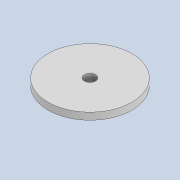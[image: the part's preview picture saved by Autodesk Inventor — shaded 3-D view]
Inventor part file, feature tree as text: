
AUTODESK INVENTOR PART (.ipt)
format: ipt  version: 2020 (Build 240168000, 168)  size: 91,136 bytes
history: native  units: mm
features: extrude x3, sketch x3
ambient origin geometry x8: Origin, YZ Plane, XZ Plane, XY Plane, X Axis, Y Axis, Z Axis, Center Point
bodies: Solid1 (feature_tree)
feature tree (6):
  extrude  "Extrusion1"  Depth=1.0mm TaperAngle=0.0deg
  extrude  "Extrusion2"  Depth=0.5mm TaperAngle=0.0deg
  extrude  "Extrusion3"  Depth=2.0mm TaperAngle=0.0deg
  sketch  "Sketch1"  dims[d0=2.7mm d1=1.0mm d2=0.0mm]
  sketch  "Sketch2"  dims[d3=6.0mm d4=0.5mm d5=0.0mm]
  sketch  "Sketch3"  dims[d6=0.8mm d7=2.0mm d8=0.0mm]
